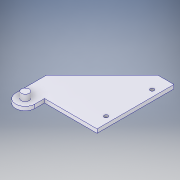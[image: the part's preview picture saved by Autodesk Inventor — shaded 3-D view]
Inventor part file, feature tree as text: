
AUTODESK INVENTOR PART (.ipt)
format: ipt  version: 2017 (Build 210142000, 142)  size: 121,856 bytes
history: native  units: in
note: dims shown in document units (in); Inventor stores cm internally (conversion verified against a paired STEP export)
features: extrude x2, sketch x2
ambient origin geometry x8: Origin, YZ Plane, XZ Plane, XY Plane, X Axis, Y Axis, Z Axis, Center Point
bodies: Solid1 (feature_tree)
feature tree (4):
  extrude  "Extrusion1"  TaperAngle=90.0deg  [1 undecoded]
  extrude  "Extrusion2"  Depth=1.6142in
  sketch  "Sketch3"  dims[d6=2.3622in d7=90.0deg]
  sketch  "Sketch4"  dims[d8=0.4929in d9=1.6142in d10=0.2953in d11=0.5906in d12=0.2362in d13=0.9456in d14=0.1181in d15=0.0in d16=0.315in d17=0.0in d18=0.1969in d19=0.4724in d20=0.4724in d21=0.1181in d22=0.1181in]
note: 1 required parameter value undecoded (feature->parameter linkage not recoverable at this tier; creation-order binding heuristic only, values carry confidence <= 0.55)
